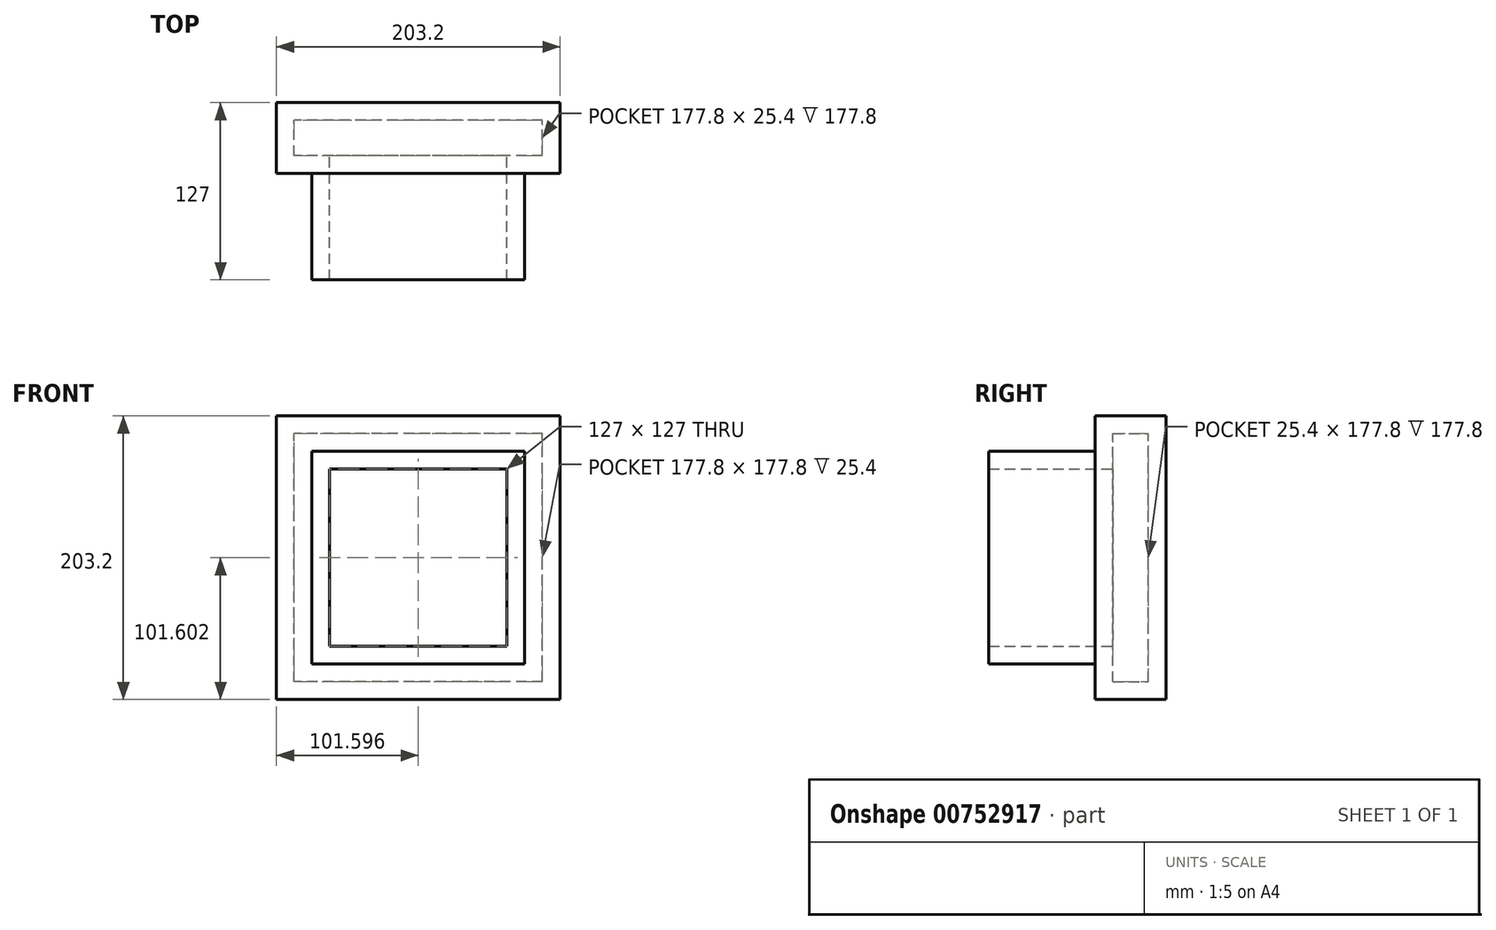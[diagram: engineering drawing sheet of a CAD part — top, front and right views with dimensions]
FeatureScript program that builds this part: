
annotation { "Feature Type Name" : "Feature", "Feature Type Description" : "" }
export const myFeature = defineFeature(function(context is Context, id is Id, definition is map)
    precondition{}
    {
        {
            var Q0;
            Q0=qCreatedBy(makeId("Front.planeOp"),FACE);
            var sketch = newSketch(context, id + "F0", { "sketchPlane" : qUnion([Q0])});
            skLineSegment(sketch, "E0", {"start": v(-63.43, 90.05) * mm, "end": v(-63.43, -62.35) * mm});
            skLineSegment(sketch, "E1", {"start": v(88.97, 90.05) * mm, "end": v(-63.43, 90.05) * mm});
            skLineSegment(sketch, "E2", {"start": v(88.97, -62.35) * mm, "end": v(88.97, 90.05) * mm});
            skLineSegment(sketch, "E3", {"start": v(-63.43, -62.35) * mm, "end": v(88.97, -62.35) * mm});
            skLineSegment(sketch, "E4", {"start": v(-63.43, -62.35) * mm, "end": v(-63.43, -87.75) * mm});
            skLineSegment(sketch, "E5", {"start": v(-63.43, -87.75) * mm, "end": v(-88.83, -87.75) * mm});
            skLineSegment(sketch, "E6", {"start": v(-88.83, -87.75) * mm, "end": v(-88.83, -62.35) * mm});
            skLineSegment(sketch, "E7", {"start": v(-88.83, -62.35) * mm, "end": v(-63.43, -62.35) * mm});
            skLineSegment(sketch, "E8", {"start": v(88.97, -62.35) * mm, "end": v(88.97, -87.75) * mm});
            skLineSegment(sketch, "E9", {"start": v(88.97, -87.75) * mm, "end": v(114.37, -87.75) * mm});
            skLineSegment(sketch, "E10", {"start": v(114.37, -87.75) * mm, "end": v(114.37, -62.35) * mm});
            skLineSegment(sketch, "E11", {"start": v(114.37, -62.35) * mm, "end": v(88.97, -62.35) * mm});
            skLineSegment(sketch, "E12", {"start": v(88.97, 90.05) * mm, "end": v(114.37, 90.05) * mm});
            skLineSegment(sketch, "E13", {"start": v(114.37, 90.05) * mm, "end": v(114.37, 115.45) * mm});
            skLineSegment(sketch, "E14", {"start": v(114.37, 115.45) * mm, "end": v(88.97, 115.45) * mm});
            skLineSegment(sketch, "E15", {"start": v(88.97, 115.45) * mm, "end": v(88.97, 90.05) * mm});
            skLineSegment(sketch, "E16", {"start": v(-63.43, 90.05) * mm, "end": v(-88.83, 90.05) * mm});
            skLineSegment(sketch, "E17", {"start": v(-88.83, 90.05) * mm, "end": v(-88.83, 115.45) * mm});
            skLineSegment(sketch, "E18", {"start": v(-88.83, 115.45) * mm, "end": v(-63.43, 115.45) * mm});
            skLineSegment(sketch, "E19", {"start": v(-63.43, 115.45) * mm, "end": v(-63.43, 90.05) * mm});
            skLineSegment(sketch, "E20", {"start": v(-88.83, 90.05) * mm, "end": v(-88.83, -62.35) * mm});
            skLineSegment(sketch, "E21", {"start": v(-63.43, -87.75) * mm, "end": v(88.97, -87.75) * mm});
            skLineSegment(sketch, "E22", {"start": v(114.37, 90.05) * mm, "end": v(114.37, -62.35) * mm});
            skLineSegment(sketch, "E23", {"start": v(-63.43, 115.45) * mm, "end": v(88.97, 115.45) * mm});
            skSolve(sketch);
        }
        {
            var Q0;
            Q0=makeQuery(id+"F0.imprint","IMPRINT",FACE,{"disambiguationData":[TD([[makeQuery(id+"F0.imprint","IMPRINT",EDGE,{"derivedFrom":sQuery(id+"F0.wireOp",EDGE,"E0")}),1.0]])]});
            extrude(context, id + "F1", {"entities" : qUnion([Q0]), "depth" : 127 * mm, "offsetDistance" : 25.4 * mm});
        }
        {
            var Q0;
            Q0 = qSketchRegion(id + "F0", true);
            extrude(context, id + "F2", {"entities" : qUnion([Q0]), "operationType" : NewBodyOperationType.ADD, "depth" : 50.8 * mm, "offsetDistance" : 25.4 * mm});
        }
        {
            var Q0;
            Q0=makeQuery(id+"F1.opExtrude","CAP_FACE",FACE,{"disambiguationData":[OSD([sQuery(id+"F0.wireOp",EDGE,"E0"),sQuery(id+"F0.wireOp",EDGE,"E1"),sQuery(id+"F0.wireOp",EDGE,"E2"),sQuery(id+"F0.wireOp",EDGE,"E3")])],"isStart":false});
            shell(context, id + "F3", {"entities" : qUnion([Q0]), "thickness" : 12.7 * mm});
        }
    });
